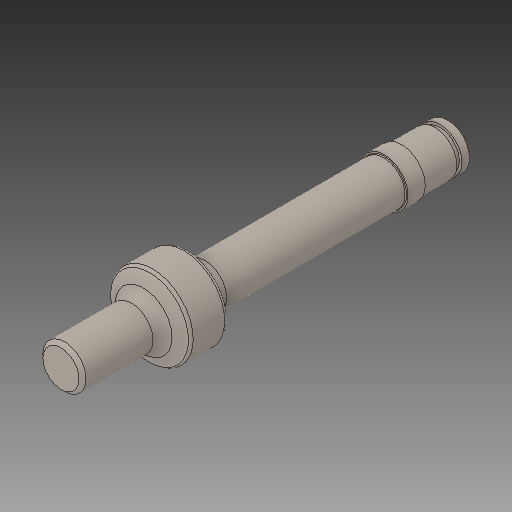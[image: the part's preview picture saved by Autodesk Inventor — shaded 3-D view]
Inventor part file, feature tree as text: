
AUTODESK INVENTOR PART (.ipt)
format: ipt  version: 2017 (Build 210142000, 142)  size: 152,064 bytes
history: native  units: in
note: dims shown in document units (in); Inventor stores cm internally (conversion verified against a paired STEP export)
features: fillet x1
ambient origin geometry x8: Origin, YZ Plane, XZ Plane, XY Plane, X Axis, Y Axis, Z Axis, Center Point
bodies: Solid1 (feature_tree)
feature tree (1):
  fillet  "Fillet2"  [1 undecoded]
note: 1 required parameter value undecoded (feature->parameter linkage not recoverable at this tier; creation-order binding heuristic only, values carry confidence <= 0.55)
